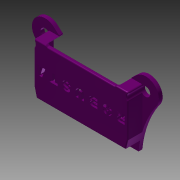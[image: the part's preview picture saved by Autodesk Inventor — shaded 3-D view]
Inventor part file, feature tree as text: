
AUTODESK INVENTOR PART (.ipt)
format: ipt  version: 2015 (Build 190159000, 159)  size: 722,944 bytes
history: native  units: mm
features: extrude x16, sketch x16, fillet x6, projected_geometry x5, plane x2
ambient origin geometry x8: Origin, YZ Plane, XZ Plane, XY Plane, X Axis, Y Axis, Z Axis, Center Point
bodies: Solid1 (feature_tree)
feature tree (45):
  extrude  "Extrusion1"  Depth=1.0mm
  extrude  "Extrusion2"  Depth=1.0mm
  extrude  "Extrusion3"  Depth=3.5mm TaperAngle=0.0deg
  extrude  "Extrusion4"  Depth=13.5mm TaperAngle=0.0deg
  extrude  "Extrusion5"  Depth=13.5mm TaperAngle=0.0deg
  extrude  "Extrusion6"  Depth=13.5mm TaperAngle=0.0deg
  extrude  "Extrusion7"  Depth=13.5mm TaperAngle=0.0deg
  extrude  "Extrusion8"  Depth=13.5mm TaperAngle=0.0deg
  plane  "Work Plane1"
  extrude  "Extrusion9"  Depth=13.5mm TaperAngle=0.0deg
  extrude  "Extrusion10"  Depth=3.5mm TaperAngle=0.0deg
  extrude  "Extrusion11"  Depth=3.5mm TaperAngle=0.0deg
  fillet  "Fillet1"  Radius=1.0mm
  fillet  "Fillet2"  Radius=1.0mm
  fillet  "Fillet3"  Radius=1.0mm
  fillet  "Fillet4"  Radius=1.0mm
  fillet  "Fillet5"  Radius=1.0mm
  fillet  "Fillet6"  Radius=1.0mm
  plane  "Work Plane2"
  extrude  "Extrusion12"  Depth=4.125mm
  extrude  "Extrusion13"  TaperAngle=45.0deg  [1 undecoded]
  sketch  "Sketch18"  dims[d47=50.0mm d48=0.0mm d49=3.178712mm d50=26.452487mm]
  extrude  "Extrusion16"  Depth=3.178712mm
  extrude  "Extrusion18"  TaperAngle=90.0deg  [1 undecoded]
  extrude  "Extrusion19"  Depth=3.5mm
  sketch  "Sketch1"  dims[d0=1.0mm d1=1.0mm]
  sketch  "Sketch3"  dims[d2=1.0mm d3=1.0mm]
  sketch  "Sketch4"  dims[d4=1.0mm d6=3.5mm d7=0.0mm]
  sketch  "Sketch5"  dims[d9=180.0deg d10=13.5mm d11=0.0mm]
  sketch  "Sketch6"  dims[d12=90.0deg d13=13.5mm d14=0.0mm]
  sketch  "Sketch7"  dims[d15=90.0deg d16=13.5mm d17=0.0mm]
  sketch  "Sketch8"  dims[d18=13.5mm d19=0.0mm d20=13.5mm d21=0.0mm]
  sketch  "Sketch9"  dims[d22=1.0mm d23=13.5mm d24=0.0mm]
  sketch  "Sketch10"  dims[d25=1.0mm d26=13.5mm d27=0.0mm]
  sketch  "Sketch11"  dims[d28=-13.5mm d29=3.5mm d30=0.0mm]
  projected_geometry  "Projected Loop1"
  sketch  "Sketch12"  dims[d31=3.5mm d32=0.0mm d33=3.5mm d34=0.0mm d35=1.0mm d38=1.0mm d39=1.0mm d40=1.0mm d41=1.0mm d42=1.0mm]
  projected_geometry  "Projected Loop2"
  sketch  "Sketch15"  dims[d43=0.0mm d44=4.125mm]
  sketch  "Sketch16"  dims[d45=90.0deg d46=45.0deg]
  projected_geometry  "Projected Loop4"
  projected_geometry  "Projected Loop5"
  projected_geometry  "Projected Loop6"
  sketch  "Sketch19"  dims[d51=50.0mm d52=0.0mm d61=90.0deg]
  sketch  "Sketch20"  dims[d64=1.0mm d65=1.0mm d68=1.0mm d69=1.0mm d73=3.5mm d74=0.0mm d83=0.25mm d84=0.25mm d85=0.25mm d86=3.5mm d87=0.0mm d90=0.75mm d91=3.5mm d92=0.0mm]
note: 2 required parameter values undecoded (feature->parameter linkage not recoverable at this tier; creation-order binding heuristic only, values carry confidence <= 0.55)
